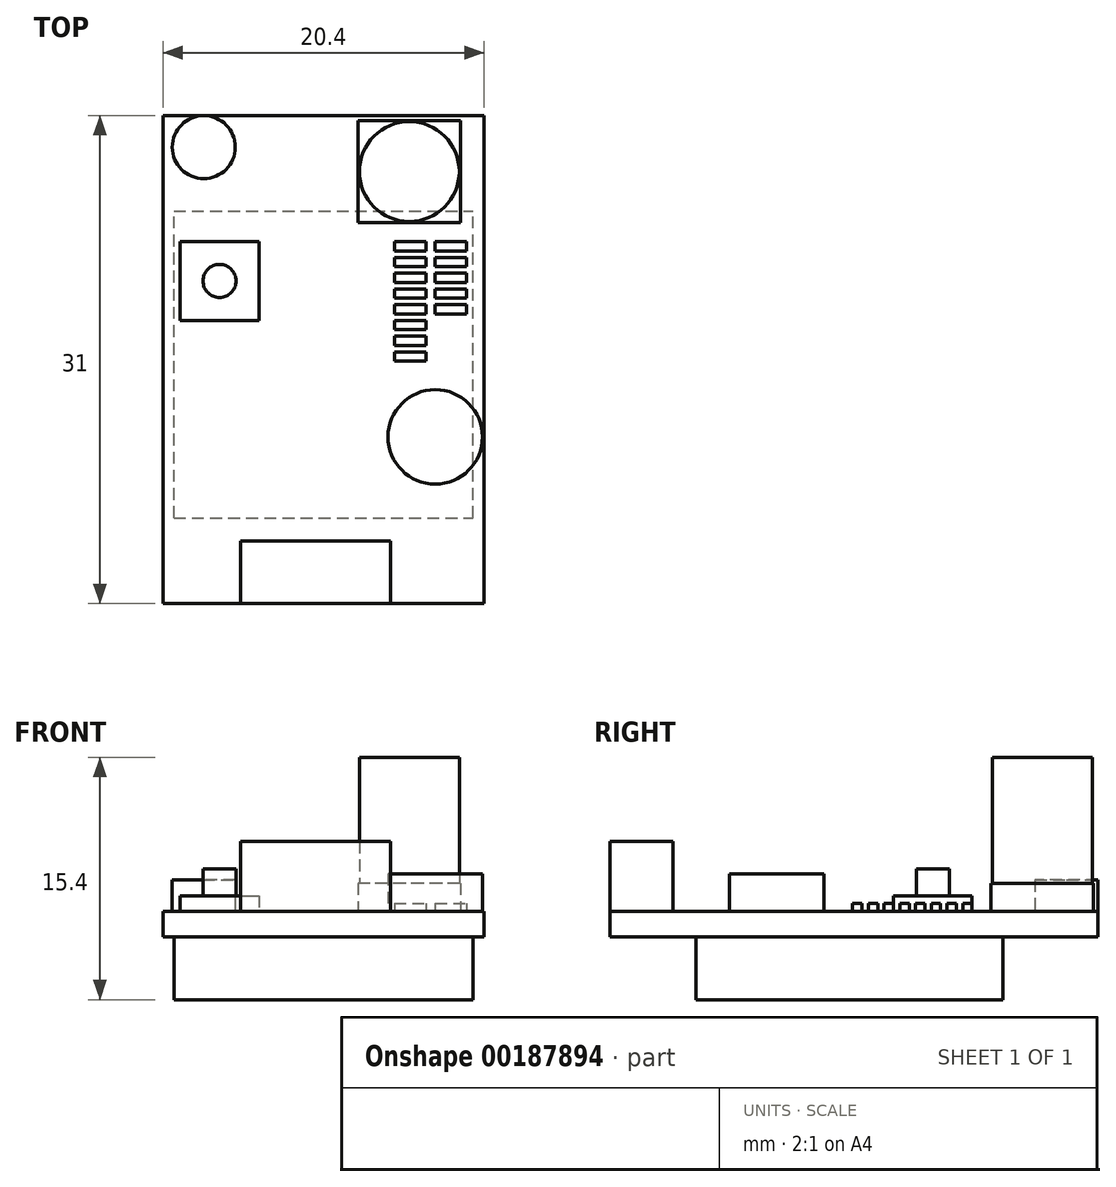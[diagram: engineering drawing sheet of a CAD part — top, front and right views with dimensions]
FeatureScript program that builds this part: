
annotation { "Feature Type Name" : "Feature", "Feature Type Description" : "" }
export const myFeature = defineFeature(function(context is Context, id is Id, definition is map)
    precondition{}
    {
        {
            var Q0;
            Q0=qCreatedBy(makeId("Top.planeOp"),FACE);
            var sketch = newSketch(context, id + "F0", { "sketchPlane" : qUnion([Q0])});
            skLineSegment(sketch, "E0.bottom", {"start": v(10.2, -15.5) * mm, "end": v(-10.2, -15.5) * mm});
            skLineSegment(sketch, "E0.top", {"start": v(10.2, 15.5) * mm, "end": v(-10.2, 15.5) * mm});
            skLineSegment(sketch, "E0.left", {"start": v(10.2, -15.5) * mm, "end": v(10.2, 15.5) * mm});
            skLineSegment(sketch, "E0.right", {"start": v(-10.2, -15.5) * mm, "end": v(-10.2, 15.5) * mm});
            skPoint(sketch, "E0.middle", {"position": v(0, 0) * mm});
            skSolve(sketch);
        }
        {
            var Q0;
            Q0=makeQuery(id+"F0.imprint","IMPRINT",FACE,{"disambiguationData":[TD([[makeQuery(id+"F0.imprint","IMPRINT",EDGE,{"derivedFrom":sQuery(id+"F0.wireOp",EDGE,"E0.bottom")}),-1.0]])]});
            extrude(context, id + "F1", {"entities" : qUnion([Q0]), "depth" : 1.6 * mm});
        }
        {
            var Q0;
            Q0=makeQuery(id+"F1.opExtrude","CAP_FACE",FACE,{"disambiguationData":[OSD([sQuery(id+"F0.wireOp",EDGE,"E0.bottom"),sQuery(id+"F0.wireOp",EDGE,"E0.top"),sQuery(id+"F0.wireOp",EDGE,"E0.left"),sQuery(id+"F0.wireOp",EDGE,"E0.right")])],"isStart":false});
            var sketch = newSketch(context, id + "F2", { "sketchPlane" : qUnion([Q0])});
            skLineSegment(sketch, "E1.bottom", {"start": v(8.7, 15.2) * mm, "end": v(2.2, 15.2) * mm});
            skLineSegment(sketch, "E1.top", {"start": v(8.7, 8.7) * mm, "end": v(2.2, 8.7) * mm});
            skLineSegment(sketch, "E1.left", {"start": v(8.7, 15.2) * mm, "end": v(8.7, 8.7) * mm});
            skLineSegment(sketch, "E1.right", {"start": v(2.2, 15.2) * mm, "end": v(2.2, 8.7) * mm});
            skSolve(sketch);
        }
        {
            var Q0;
            Q0 = qSketchRegion(id + "F2", true);
            extrude(context, id + "F3", {"entities" : qUnion([Q0]), "depth" : 1.8 * mm});
        }
        {
            var Q0;
            Q0=makeQuery(id+"F3.opExtrude","CAP_FACE",FACE,{"disambiguationData":[OSD([sQuery(id+"F2.wireOp",EDGE,"E1.bottom"),sQuery(id+"F2.wireOp",EDGE,"E1.top"),sQuery(id+"F2.wireOp",EDGE,"E1.left"),sQuery(id+"F2.wireOp",EDGE,"E1.right")])],"isStart":false});
            var sketch = newSketch(context, id + "F4", { "sketchPlane" : qUnion([Q0])});
            skCircle(sketch, "E2", {"center": v(5.45, 11.95) * mm, "radius": 3.18 * mm});
            skLineSegment(sketch, "E3", {"start": v(2.2, 8.7) * mm, "end": v(8.7, 15.2) * mm, "construction": true});
            skSolve(sketch);
        }
        {
            var Q0;
            Q0 = qSketchRegion(id + "F4", true);
            extrude(context, id + "F5", {"entities" : qUnion([Q0]), "operationType" : NewBodyOperationType.ADD, "depth" : 8 * mm});
        }
        {
            var Q0;
            Q0=makeQuery(id+"F1.opExtrude","CAP_FACE",FACE,{"disambiguationData":[OSD([sQuery(id+"F0.wireOp",EDGE,"E0.bottom"),sQuery(id+"F0.wireOp",EDGE,"E0.top"),sQuery(id+"F0.wireOp",EDGE,"E0.left"),sQuery(id+"F0.wireOp",EDGE,"E0.right")])],"isStart":false});
            var sketch = newSketch(context, id + "F6", { "sketchPlane" : qUnion([Q0])});
            skCircle(sketch, "E4", {"center": v(-7.6, 13.5) * mm, "radius": 2 * mm});
            skSolve(sketch);
        }
        {
            var Q0;
            Q0 = qSketchRegion(id + "F6", true);
            extrude(context, id + "F7", {"entities" : qUnion([Q0]), "depth" : 2 * mm});
        }
        {
            var Q0;
            Q0=makeQuery(id+"F1.opExtrude","CAP_FACE",FACE,{"disambiguationData":[OSD([sQuery(id+"F0.wireOp",EDGE,"E0.bottom"),sQuery(id+"F0.wireOp",EDGE,"E0.top"),sQuery(id+"F0.wireOp",EDGE,"E0.left"),sQuery(id+"F0.wireOp",EDGE,"E0.right")])],"isStart":false});
            var sketch = newSketch(context, id + "F8", { "sketchPlane" : qUnion([Q0])});
            skLineSegment(sketch, "E5.bottom", {"start": v(-5.25, -15.5) * mm, "end": v(4.25, -15.5) * mm});
            skLineSegment(sketch, "E5.top", {"start": v(-5.25, -11.5) * mm, "end": v(4.25, -11.5) * mm});
            skLineSegment(sketch, "E5.left", {"start": v(-5.25, -15.5) * mm, "end": v(-5.25, -11.5) * mm});
            skLineSegment(sketch, "E5.right", {"start": v(4.25, -15.5) * mm, "end": v(4.25, -11.5) * mm});
            skSolve(sketch);
        }
        {
            var Q0;
            Q0 = qSketchRegion(id + "F8", true);
            extrude(context, id + "F9", {"entities" : qUnion([Q0]), "depth" : (6.05 - 1.6) * mm});
        }
        {
            var Q0;
            Q0=makeQuery(id+"F1.opExtrude","CAP_FACE",FACE,{"disambiguationData":[OSD([sQuery(id+"F0.wireOp",EDGE,"E0.bottom"),sQuery(id+"F0.wireOp",EDGE,"E0.top"),sQuery(id+"F0.wireOp",EDGE,"E0.left"),sQuery(id+"F0.wireOp",EDGE,"E0.right")])],"isStart":false});
            var sketch = newSketch(context, id + "F10", { "sketchPlane" : qUnion([Q0])});
            skLineSegment(sketch, "E6.bottom", {"start": v(-9.1, 7.5) * mm, "end": v(-4.1, 7.5) * mm});
            skLineSegment(sketch, "E6.top", {"start": v(-9.1, 2.5) * mm, "end": v(-4.1, 2.5) * mm});
            skLineSegment(sketch, "E6.left", {"start": v(-9.1, 7.5) * mm, "end": v(-9.1, 2.5) * mm});
            skLineSegment(sketch, "E6.right", {"start": v(-4.1, 7.5) * mm, "end": v(-4.1, 2.5) * mm});
            skSolve(sketch);
        }
        {
            var Q0;
            Q0 = qSketchRegion(id + "F10", true);
            extrude(context, id + "F11", {"entities" : qUnion([Q0]), "depth" : 1 * mm});
        }
        {
            var Q0;
            Q0=makeQuery(id+"F11.opExtrude","CAP_FACE",FACE,{"disambiguationData":[OSD([sQuery(id+"F10.wireOp",EDGE,"E6.bottom"),sQuery(id+"F10.wireOp",EDGE,"E6.top"),sQuery(id+"F10.wireOp",EDGE,"E6.left"),sQuery(id+"F10.wireOp",EDGE,"E6.right")])],"isStart":false});
            var sketch = newSketch(context, id + "F12", { "sketchPlane" : qUnion([Q0])});
            skCircle(sketch, "E7", {"center": v(-6.6, 5) * mm, "radius": 1.05 * mm});
            skPoint(sketch, "E7.centerSnap0", {"position": v(-6.6, 2.5) * mm});
            skLineSegment(sketch, "E8", {"start": v(-9.1, 2.5) * mm, "end": v(-4.1, 7.5) * mm, "construction": true});
            skSolve(sketch);
        }
        {
            var Q0;
            Q0 = qSketchRegion(id + "F12", true);
            extrude(context, id + "F13", {"entities" : qUnion([Q0]), "operationType" : NewBodyOperationType.ADD, "depth" : 1.7 * mm});
        }
        {
            var Q0;
            Q0=makeQuery(id+"F1.opExtrude","CAP_FACE",FACE,{"disambiguationData":[OSD([sQuery(id+"F0.wireOp",EDGE,"E0.bottom"),sQuery(id+"F0.wireOp",EDGE,"E0.top"),sQuery(id+"F0.wireOp",EDGE,"E0.left"),sQuery(id+"F0.wireOp",EDGE,"E0.right")])],"isStart":false});
            var sketch = newSketch(context, id + "F14", { "sketchPlane" : qUnion([Q0])});
            skCircle(sketch, "E9", {"center": v(7.1, -4.9) * mm, "radius": 3 * mm});
            skSolve(sketch);
        }
        {
            var Q0;
            Q0 = qSketchRegion(id + "F14", true);
            extrude(context, id + "F15", {"entities" : qUnion([Q0]), "depth" : 2.4 * mm});
        }
        {
            var Q0;
            Q0=makeQuery(id+"F1.opExtrude","CAP_FACE",FACE,{"disambiguationData":[OSD([sQuery(id+"F0.wireOp",EDGE,"E0.bottom"),sQuery(id+"F0.wireOp",EDGE,"E0.top"),sQuery(id+"F0.wireOp",EDGE,"E0.left"),sQuery(id+"F0.wireOp",EDGE,"E0.right")])],"isStart":true});
            var sketch = newSketch(context, id + "F16", { "sketchPlane" : qUnion([Q0])});
            skLineSegment(sketch, "E10.bottom", {"start": v(-9.5, 10.05) * mm, "end": v(9.5, 10.05) * mm});
            skLineSegment(sketch, "E10.top", {"start": v(-9.5, -9.45) * mm, "end": v(9.5, -9.45) * mm});
            skLineSegment(sketch, "E10.left", {"start": v(-9.5, 10.05) * mm, "end": v(-9.5, -9.45) * mm});
            skLineSegment(sketch, "E10.right", {"start": v(9.5, 10.05) * mm, "end": v(9.5, -9.45) * mm});
            skLineSegment(sketch, "E11", {"start": v(0, -9.45) * mm, "end": v(0, -15.5) * mm, "construction": true});
            skSolve(sketch);
        }
        {
            var Q0;
            Q0 = qSketchRegion(id + "F16", true);
            extrude(context, id + "F17", {"entities" : qUnion([Q0]), "depth" : 4 * mm});
        }
        {
            var Q0;
            Q0=makeQuery(id+"F1.opExtrude","CAP_FACE",FACE,{"disambiguationData":[OSD([sQuery(id+"F0.wireOp",EDGE,"E0.bottom"),sQuery(id+"F0.wireOp",EDGE,"E0.top"),sQuery(id+"F0.wireOp",EDGE,"E0.left"),sQuery(id+"F0.wireOp",EDGE,"E0.right")])],"isStart":false});
            var sketch = newSketch(context, id + "F18", { "sketchPlane" : qUnion([Q0])});
            skLineSegment(sketch, "E12.bottom", {"start": v(7.1, 7.5) * mm, "end": v(9.1, 7.5) * mm});
            skLineSegment(sketch, "E12.top", {"start": v(7.1, 6.9) * mm, "end": v(9.1, 6.9) * mm});
            skLineSegment(sketch, "E12.left", {"start": v(7.1, 7.5) * mm, "end": v(7.1, 6.9) * mm});
            skLineSegment(sketch, "E12.right", {"start": v(9.1, 7.5) * mm, "end": v(9.1, 6.9) * mm});
            skLineSegment(sketch, "E13.1.0.0", {"start": v(7.1, 5.9) * mm, "end": v(9.1, 5.9) * mm});
            skLineSegment(sketch, "E13.1.0.1", {"start": v(7.1, 6.5) * mm, "end": v(9.1, 6.5) * mm});
            skLineSegment(sketch, "E13.1.0.2", {"start": v(9.1, 6.5) * mm, "end": v(9.1, 5.9) * mm});
            skLineSegment(sketch, "E13.1.0.3", {"start": v(7.1, 6.5) * mm, "end": v(7.1, 5.9) * mm});
            skLineSegment(sketch, "E13.2.0.0", {"start": v(7.1, 4.9) * mm, "end": v(9.1, 4.9) * mm});
            skLineSegment(sketch, "E13.2.0.1", {"start": v(7.1, 5.5) * mm, "end": v(9.1, 5.5) * mm});
            skLineSegment(sketch, "E13.2.0.2", {"start": v(9.1, 5.5) * mm, "end": v(9.1, 4.9) * mm});
            skLineSegment(sketch, "E13.2.0.3", {"start": v(7.1, 5.5) * mm, "end": v(7.1, 4.9) * mm});
            skLineSegment(sketch, "E13.3.0.0", {"start": v(7.1, 3.9) * mm, "end": v(9.1, 3.9) * mm});
            skLineSegment(sketch, "E13.3.0.1", {"start": v(7.1, 4.5) * mm, "end": v(9.1, 4.5) * mm});
            skLineSegment(sketch, "E13.3.0.2", {"start": v(9.1, 4.5) * mm, "end": v(9.1, 3.9) * mm});
            skLineSegment(sketch, "E13.3.0.3", {"start": v(7.1, 4.5) * mm, "end": v(7.1, 3.9) * mm});
            skLineSegment(sketch, "E13.4.0.0", {"start": v(7.1, 2.9) * mm, "end": v(9.1, 2.9) * mm});
            skLineSegment(sketch, "E13.4.0.1", {"start": v(7.1, 3.5) * mm, "end": v(9.1, 3.5) * mm});
            skLineSegment(sketch, "E13.4.0.2", {"start": v(9.1, 3.5) * mm, "end": v(9.1, 2.9) * mm});
            skLineSegment(sketch, "E13.4.0.3", {"start": v(7.1, 3.5) * mm, "end": v(7.1, 2.9) * mm});
            skLineSegment(sketch, "E13.direction1", {"start": v(7.1, 6.9) * mm, "end": v(7.1, 5.9) * mm, "construction": true});
            skLineSegment(sketch, "E14.bottom", {"start": v(4.5, 7.5) * mm, "end": v(6.5, 7.5) * mm});
            skLineSegment(sketch, "E14.top", {"start": v(4.5, 6.9) * mm, "end": v(6.5, 6.9) * mm});
            skLineSegment(sketch, "E14.left", {"start": v(4.5, 7.5) * mm, "end": v(4.5, 6.9) * mm});
            skLineSegment(sketch, "E14.right", {"start": v(6.5, 7.5) * mm, "end": v(6.5, 6.9) * mm});
            skLineSegment(sketch, "E15.1.0.0", {"start": v(4.5, 6.5) * mm, "end": v(4.5, 5.9) * mm});
            skLineSegment(sketch, "E15.1.0.1", {"start": v(4.5, 6.5) * mm, "end": v(6.5, 6.5) * mm});
            skLineSegment(sketch, "E15.1.0.2", {"start": v(6.5, 6.5) * mm, "end": v(6.5, 5.9) * mm});
            skLineSegment(sketch, "E15.1.0.3", {"start": v(4.5, 5.9) * mm, "end": v(6.5, 5.9) * mm});
            skLineSegment(sketch, "E15.2.0.0", {"start": v(4.5, 5.5) * mm, "end": v(4.5, 4.9) * mm});
            skLineSegment(sketch, "E15.2.0.1", {"start": v(4.5, 5.5) * mm, "end": v(6.5, 5.5) * mm});
            skLineSegment(sketch, "E15.2.0.2", {"start": v(6.5, 5.5) * mm, "end": v(6.5, 4.9) * mm});
            skLineSegment(sketch, "E15.2.0.3", {"start": v(4.5, 4.9) * mm, "end": v(6.5, 4.9) * mm});
            skLineSegment(sketch, "E15.3.0.0", {"start": v(4.5, 4.5) * mm, "end": v(4.5, 3.9) * mm});
            skLineSegment(sketch, "E15.3.0.1", {"start": v(4.5, 4.5) * mm, "end": v(6.5, 4.5) * mm});
            skLineSegment(sketch, "E15.3.0.2", {"start": v(6.5, 4.5) * mm, "end": v(6.5, 3.9) * mm});
            skLineSegment(sketch, "E15.3.0.3", {"start": v(4.5, 3.9) * mm, "end": v(6.5, 3.9) * mm});
            skLineSegment(sketch, "E15.4.0.0", {"start": v(4.5, 3.5) * mm, "end": v(4.5, 2.9) * mm});
            skLineSegment(sketch, "E15.4.0.1", {"start": v(4.5, 3.5) * mm, "end": v(6.5, 3.5) * mm});
            skLineSegment(sketch, "E15.4.0.2", {"start": v(6.5, 3.5) * mm, "end": v(6.5, 2.9) * mm});
            skLineSegment(sketch, "E15.4.0.3", {"start": v(4.5, 2.9) * mm, "end": v(6.5, 2.9) * mm});
            skLineSegment(sketch, "E15.5.0.0", {"start": v(4.5, 2.5) * mm, "end": v(4.5, 1.9) * mm});
            skLineSegment(sketch, "E15.5.0.1", {"start": v(4.5, 2.5) * mm, "end": v(6.5, 2.5) * mm});
            skLineSegment(sketch, "E15.5.0.2", {"start": v(6.5, 2.5) * mm, "end": v(6.5, 1.9) * mm});
            skLineSegment(sketch, "E15.5.0.3", {"start": v(4.5, 1.9) * mm, "end": v(6.5, 1.9) * mm});
            skLineSegment(sketch, "E15.6.0.0", {"start": v(4.5, 1.5) * mm, "end": v(4.5, 0.9) * mm});
            skLineSegment(sketch, "E15.6.0.1", {"start": v(4.5, 1.5) * mm, "end": v(6.5, 1.5) * mm});
            skLineSegment(sketch, "E15.6.0.2", {"start": v(6.5, 1.5) * mm, "end": v(6.5, 0.9) * mm});
            skLineSegment(sketch, "E15.6.0.3", {"start": v(4.5, 0.9) * mm, "end": v(6.5, 0.9) * mm});
            skLineSegment(sketch, "E15.7.0.0", {"start": v(4.5, 0.5) * mm, "end": v(4.5, -0.1) * mm});
            skLineSegment(sketch, "E15.7.0.1", {"start": v(4.5, 0.5) * mm, "end": v(6.5, 0.5) * mm});
            skLineSegment(sketch, "E15.7.0.2", {"start": v(6.5, 0.5) * mm, "end": v(6.5, -0.1) * mm});
            skLineSegment(sketch, "E15.7.0.3", {"start": v(4.5, -0.1) * mm, "end": v(6.5, -0.1) * mm});
            skLineSegment(sketch, "E15.direction1", {"start": v(4.5, 6.9) * mm, "end": v(4.5, 5.9) * mm, "construction": true});
            skSolve(sketch);
        }
        {
            var Q0;
            Q0 = qSketchRegion(id + "F18", true);
            extrude(context, id + "F19", {"entities" : qUnion([Q0]), "depth" : 0.5 * mm});
        }
    });
